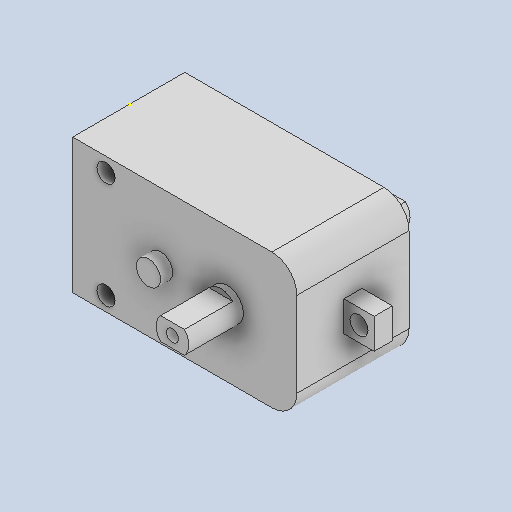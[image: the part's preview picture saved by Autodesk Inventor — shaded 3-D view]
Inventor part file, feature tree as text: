
AUTODESK INVENTOR PART (.ipt)
format: ipt  version: 2022 (Build 260153070, 153G)  size: 202,240 bytes
history: native  units: in
note: dims shown in document units (in); Inventor stores cm internally (conversion verified against a paired STEP export)
features: extrude x8, sketch x6, other x2, plane x2
ambient origin geometry x8: Origin, YZ Plane, XZ Plane, XY Plane, X Axis, Y Axis, Z Axis, Center Point
bodies: Solid1 (feature_tree)
feature tree (18):
  sketch  "Sketch1"  dims[d6=0.1575in d8=0.1181in d11=0.2165in]
  extrude  "Extrusion1"  Depth=0.1181in
  extrude  "Extrusion2"  Depth=0.3445in
  extrude  "Extrusion3"  Depth=0.5512in
  extrude  "Extrusion4"  Depth=0.1457in
  sketch  "Sketch2"  dims[d12=0.876in d13=0.3445in]
  extrude  "Extrusion5"  Depth=0.8858in TaperAngle=0.0deg
  extrude  "Extrusion6"  Depth=1.437in TaperAngle=0.0deg
  extrude  "Extrusion7"  Depth=0.1969in
  extrude  "Extrusion8"  Depth=0.1969in
  other  "Work Point1"
  sketch  "Sketch3"  dims[d16=0.5709in d17=0.5512in]
  sketch  "Sketch4"  dims[d18=1.4567in d19=0.1457in]
  sketch  "Sketch5"  dims[d20=0.7283in d21=0.0in d22=0.8858in d23=0.0in]
  sketch  "Sketch6"  dims[d24=0.8071in d25=0.0in d26=1.437in d27=0.0in d28=0.2126in d29=0.4539in d30=0.0787in d31=0.1969in d32=0.0in d33=0.0787in d34=0.1969in d35=0.0in d36=0.1181in d37=0.1969in d38=0.3346in d39=0.1969in d40=0.0in d41=0.1181in d42=0.1969in d43=0.0in]
  plane  "Work Plane1"
  plane  "Work Plane2"
  other  "Work Axis1"
